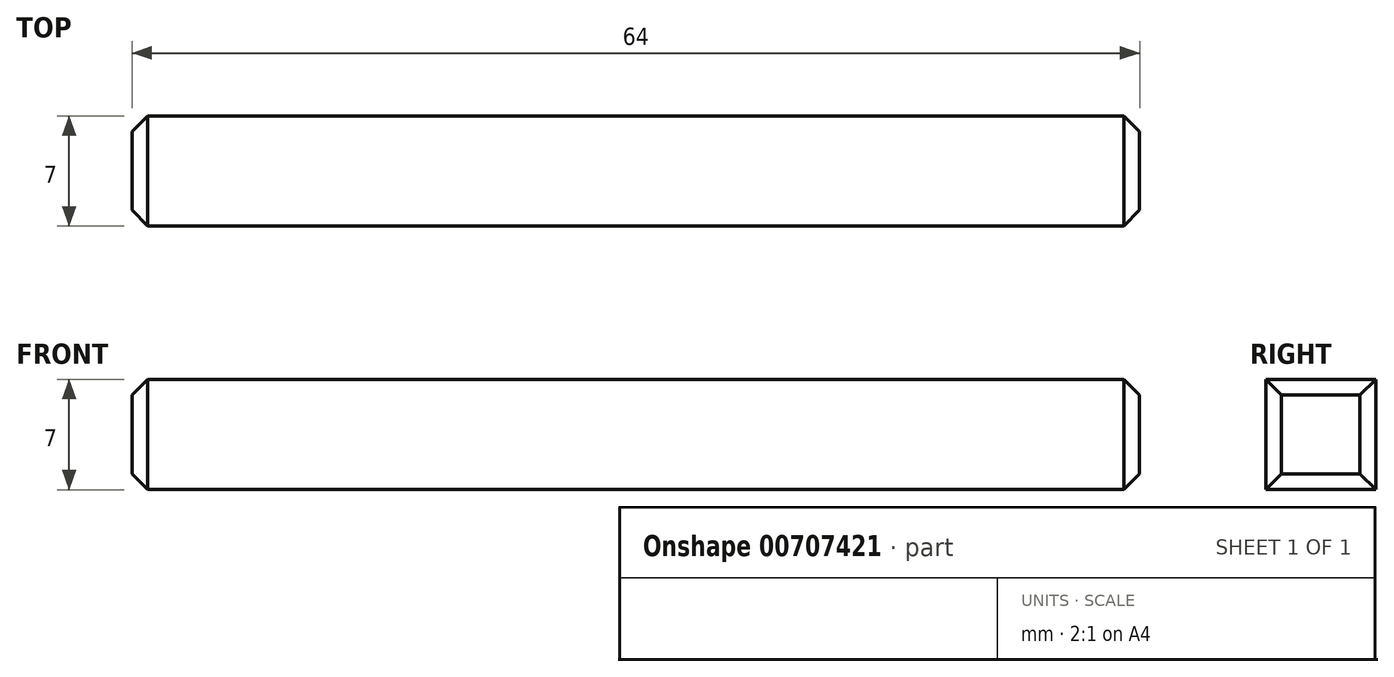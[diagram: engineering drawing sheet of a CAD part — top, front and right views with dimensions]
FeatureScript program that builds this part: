
annotation { "Feature Type Name" : "Feature", "Feature Type Description" : "" }
export const myFeature = defineFeature(function(context is Context, id is Id, definition is map)
    precondition{}
    {
        {
            var Q0;
            Q0=qCreatedBy(makeId("Front.planeOp"),FACE);
            var sketch = newSketch(context, id + "F0", { "sketchPlane" : qUnion([Q0])});
            skLineSegment(sketch, "E0", {"start": v(-41.34, 10) * mm, "end": v(22.66, 10) * mm});
            skLineSegment(sketch, "E1", {"start": v(-41.34, 10) * mm, "end": v(-41.34, 3) * mm});
            skLineSegment(sketch, "E2", {"start": v(-41.34, 3) * mm, "end": v(22.66, 3) * mm});
            skLineSegment(sketch, "E3", {"start": v(22.66, 10) * mm, "end": v(22.66, 3) * mm});
            skSolve(sketch);
        }
        {
            var Q0;
            Q0=makeQuery(id+"F0.imprint","IMPRINT",FACE,{"disambiguationData":[TD([[makeQuery(id+"F0.imprint","IMPRINT",EDGE,{"derivedFrom":sQuery(id+"F0.wireOp",EDGE,"E0")}),-1.0]])]});
            extrude(context, id + "F1", {"entities" : qUnion([Q0]), "depth" : 7 * mm, "offsetDistance" : 25 * mm});
        }
        {
            var Q0;
            Q0=makeQuery(id+"F1.opExtrude","SWEPT_EDGE",EDGE,{"disambiguationData":[OSD([sQuery(id+"F0.wireOp",EDGE,"E0"),sQuery(id+"F0.wireOp",EDGE,"E3")])]});
            var Q1;
            Q1=makeQuery(id+"F1.opExtrude","CAP_EDGE",EDGE,{"disambiguationData":[OSD([sQuery(id+"F0.wireOp",EDGE,"E3")])],"isStart":false});
            var Q2;
            Q2=makeQuery(id+"F1.opExtrude","SWEPT_EDGE",EDGE,{"disambiguationData":[OSD([sQuery(id+"F0.wireOp",EDGE,"E2"),sQuery(id+"F0.wireOp",EDGE,"E3")])]});
            var Q3;
            Q3=makeQuery(id+"F1.opExtrude","CAP_EDGE",EDGE,{"disambiguationData":[OSD([sQuery(id+"F0.wireOp",EDGE,"E3")])],"isStart":true});
            chamfer(context, id + "F2", {"entities" : qUnion([Q0, Q1, Q2, Q3]), "width" : 1 * mm, "tangentPropagation" : true});
        }
        {
            var Q0;
            Q0=makeQuery(id+"F1.opExtrude","CAP_EDGE",EDGE,{"disambiguationData":[OSD([sQuery(id+"F0.wireOp",EDGE,"E1")])],"isStart":false});
            var Q1;
            Q1=makeQuery(id+"F1.opExtrude","SWEPT_EDGE",EDGE,{"disambiguationData":[OSD([sQuery(id+"F0.wireOp",EDGE,"E0"),sQuery(id+"F0.wireOp",EDGE,"E1")])]});
            var Q2;
            Q2=makeQuery(id+"F1.opExtrude","CAP_EDGE",EDGE,{"disambiguationData":[OSD([sQuery(id+"F0.wireOp",EDGE,"E1")])],"isStart":true});
            var Q3;
            Q3=makeQuery(id+"F1.opExtrude","SWEPT_EDGE",EDGE,{"disambiguationData":[OSD([sQuery(id+"F0.wireOp",EDGE,"E1"),sQuery(id+"F0.wireOp",EDGE,"E2")])]});
            chamfer(context, id + "F3", {"entities" : qUnion([Q0, Q1, Q2, Q3]), "width" : 1 * mm, "tangentPropagation" : true});
        }
    });
